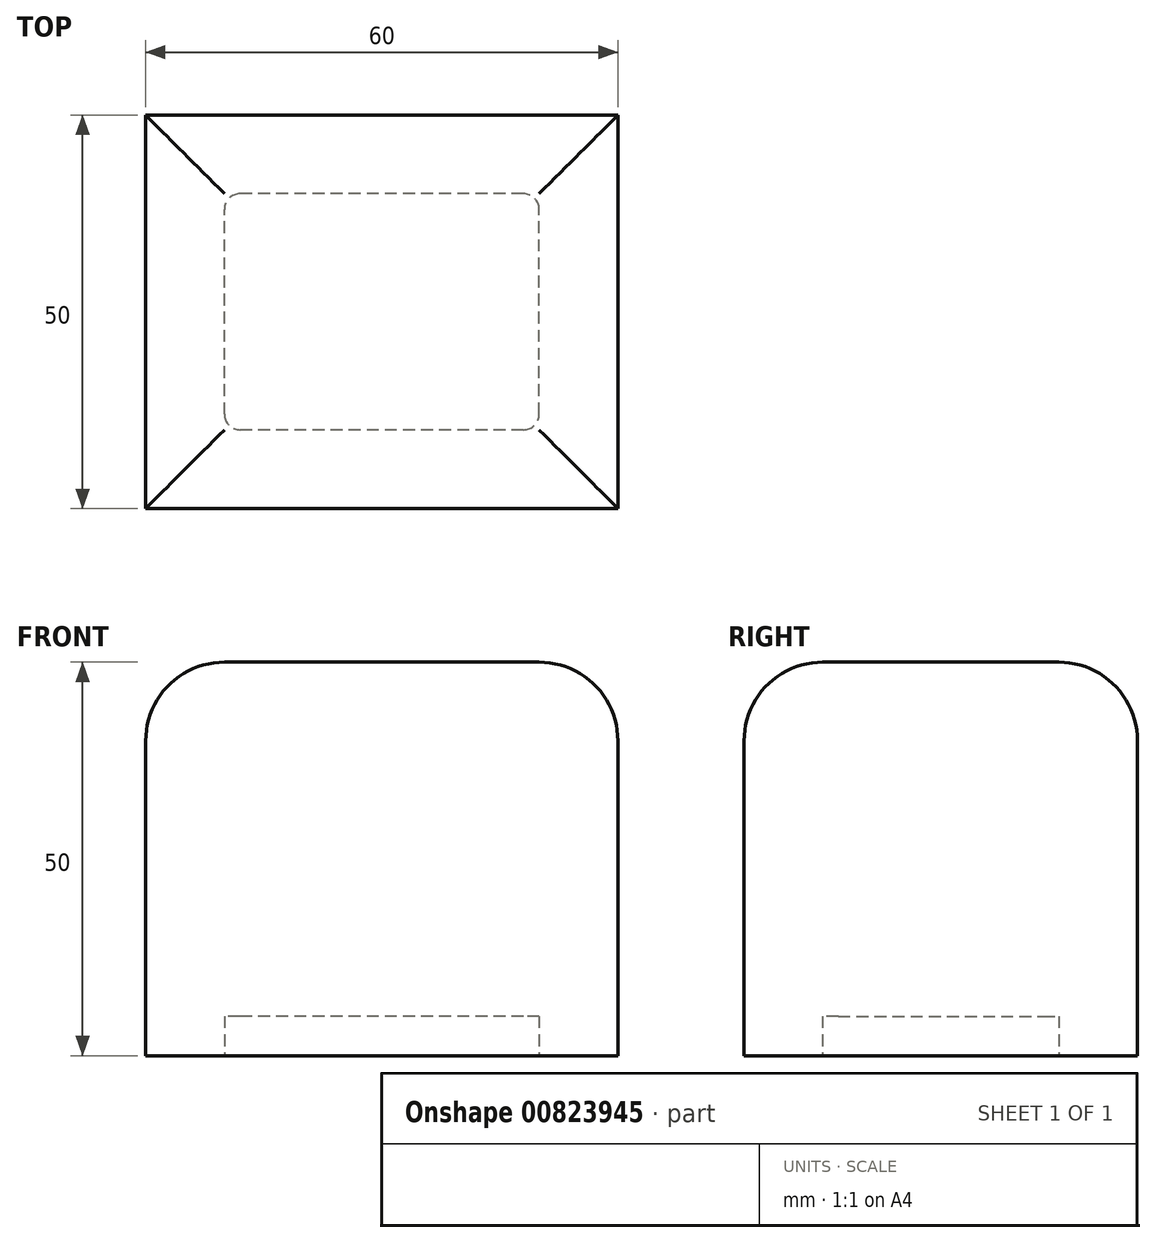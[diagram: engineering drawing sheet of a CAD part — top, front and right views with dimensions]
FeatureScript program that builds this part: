
annotation { "Feature Type Name" : "Feature", "Feature Type Description" : "" }
export const myFeature = defineFeature(function(context is Context, id is Id, definition is map)
    precondition{}
    {
        {
            var Q0;
            Q0=qCreatedBy(makeId("Top.planeOp"),FACE);
            var sketch = newSketch(context, id + "F0", { "sketchPlane" : qUnion([Q0])});
            skLineSegment(sketch, "E0.bottom", {"start": v(0, 0) * mm, "end": v(60, 0) * mm});
            skLineSegment(sketch, "E0.top", {"start": v(0, 50) * mm, "end": v(60, 50) * mm});
            skLineSegment(sketch, "E0.left", {"start": v(0, 0) * mm, "end": v(0, 50) * mm});
            skLineSegment(sketch, "E0.right", {"start": v(60, 0) * mm, "end": v(60, 50) * mm});
            skSolve(sketch);
        }
        {
            var Q0;
            Q0 = qSketchRegion(id + "F0", true);
            var Q1;
            Q1=sQuery(id+"F0.wireOp",EDGE,"E0.left");
            var Q2;
            Q2=sQuery(id+"F0.wireOp",EDGE,"E0.top");
            var Q3;
            Q3=sQuery(id+"F0.wireOp",EDGE,"E0.right");
            var Q4;
            Q4=sQuery(id+"F0.wireOp",EDGE,"E0.bottom");
            extrude(context, id + "F1", {"entities" : qUnion([Q0]), "surfaceEntities" : qUnion([Q1, Q2, Q3, Q4]), "depth" : 50 * mm, "offsetDistance" : 25 * mm});
        }
        {
            var Q0;
            Q0=makeQuery(id+"F1.opExtrude","CAP_FACE",FACE,{"disambiguationData":[OSD([sQuery(id+"F0.wireOp",EDGE,"E0.bottom"),sQuery(id+"F0.wireOp",EDGE,"E0.top"),sQuery(id+"F0.wireOp",EDGE,"E0.left"),sQuery(id+"F0.wireOp",EDGE,"E0.right")])],"isStart":true});
            var sketch = newSketch(context, id + "F2", { "sketchPlane" : qUnion([Q0])});
            skLineSegment(sketch, "E1.bottom", {"start": v(50, -10) * mm, "end": v(10, -10) * mm});
            skLineSegment(sketch, "E1.top", {"start": v(50, -40) * mm, "end": v(10, -40) * mm});
            skLineSegment(sketch, "E1.left", {"start": v(50, -10) * mm, "end": v(50, -40) * mm});
            skLineSegment(sketch, "E1.right", {"start": v(10, -10) * mm, "end": v(10, -40) * mm});
            skPoint(sketch, "E1.middle", {"position": v(30, -25) * mm});
            skPoint(sketch, "E1.middle.positionSnap0", {"position": v(0, -25) * mm});
            skPoint(sketch, "E1.middle.positionSnap1", {"position": v(30, 0) * mm});
            skPoint(sketch, "E1.centerSnap0", {"position": v(0, -25) * mm});
            skPoint(sketch, "E1.centerSnap1", {"position": v(30, 0) * mm});
            skSolve(sketch);
        }
        {
            var Q0;
            Q0=makeQuery(id+"F2.imprint","IMPRINT",FACE,{"disambiguationData":[TD([[makeQuery(id+"F2.imprint","IMPRINT",EDGE,{"derivedFrom":sQuery(id+"F2.wireOp",EDGE,"E1.bottom")}),1.0]])]});
            extrude(context, id + "F3", {"entities" : qUnion([Q0]), "operationType" : NewBodyOperationType.REMOVE, "oppositeDirection" : true, "depth" : 5 * mm, "offsetDistance" : 25 * mm});
        }
        {
            var Q0;
            Q0=makeQuery(id+"F3.boolean.opBoolean","COPY",EDGE,{"derivedFrom":makeQuery(id+"F3.opExtrude","SWEPT_EDGE",EDGE,{"disambiguationData":[OSD([sQuery(id+"F2.wireOp",EDGE,"E1.top"),sQuery(id+"F2.wireOp",EDGE,"E1.left")])]})});
            var Q1;
            Q1=makeQuery(id+"F3.boolean.opBoolean","COPY",EDGE,{"derivedFrom":makeQuery(id+"F3.opExtrude","SWEPT_EDGE",EDGE,{"disambiguationData":[OSD([sQuery(id+"F2.wireOp",EDGE,"E1.top"),sQuery(id+"F2.wireOp",EDGE,"E1.right")])]})});
            var Q2;
            Q2=makeQuery(id+"F3.boolean.opBoolean","COPY",EDGE,{"derivedFrom":makeQuery(id+"F3.opExtrude","SWEPT_EDGE",EDGE,{"disambiguationData":[OSD([sQuery(id+"F2.wireOp",EDGE,"E1.bottom"),sQuery(id+"F2.wireOp",EDGE,"E1.right")])]})});
            var Q3;
            Q3=makeQuery(id+"F3.boolean.opBoolean","COPY",EDGE,{"derivedFrom":makeQuery(id+"F3.opExtrude","SWEPT_EDGE",EDGE,{"disambiguationData":[OSD([sQuery(id+"F2.wireOp",EDGE,"E1.bottom"),sQuery(id+"F2.wireOp",EDGE,"E1.left")])]})});
            fillet(context, id + "F4", {"entities" : qUnion([Q0, Q1, Q2, Q3]), "radius" : 2 * mm, "tangentPropagation" : true, "allowEdgeOverflow" : false});
        }
        {
            var Q0;
            Q0=makeQuery(id+"F1.opExtrude","CAP_FACE",FACE,{"disambiguationData":[OSD([sQuery(id+"F0.wireOp",EDGE,"E0.bottom"),sQuery(id+"F0.wireOp",EDGE,"E0.top"),sQuery(id+"F0.wireOp",EDGE,"E0.left"),sQuery(id+"F0.wireOp",EDGE,"E0.right")])],"isStart":false});
            fillet(context, id + "F5", {"entities" : qUnion([Q0]), "radius" : 10 * mm, "tangentPropagation" : true, "allowEdgeOverflow" : false});
        }
    });
